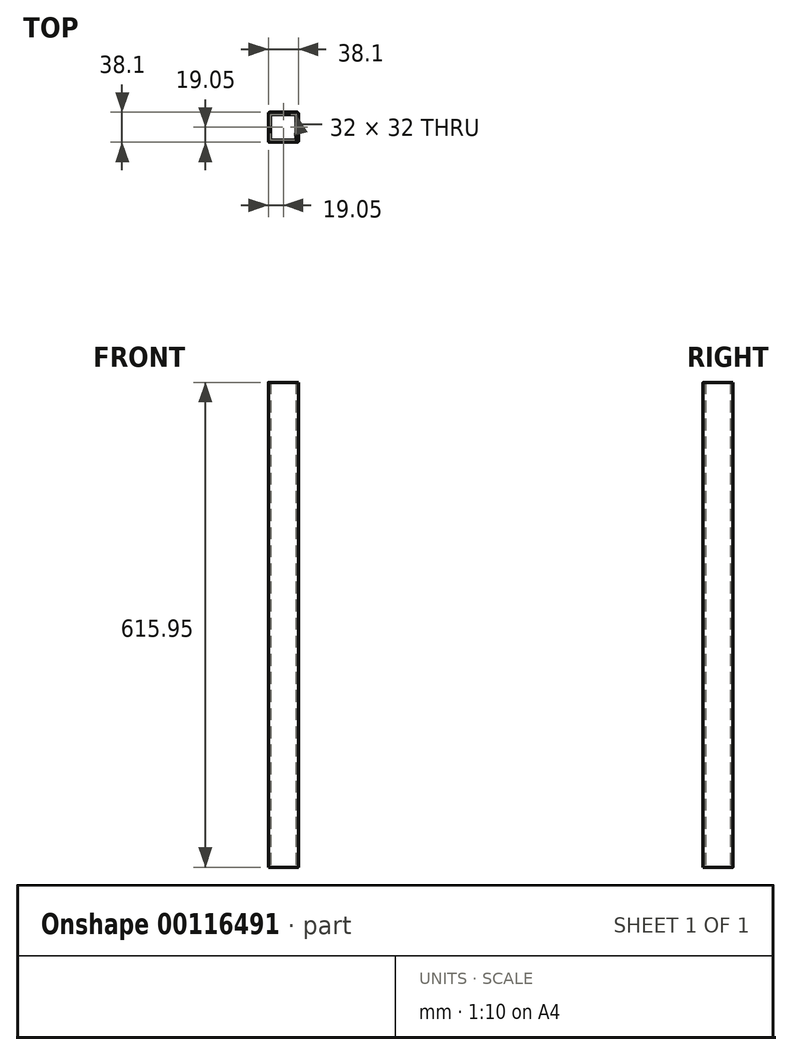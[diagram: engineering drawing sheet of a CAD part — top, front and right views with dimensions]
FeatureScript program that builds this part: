
annotation { "Feature Type Name" : "Feature", "Feature Type Description" : "" }
export const myFeature = defineFeature(function(context is Context, id is Id, definition is map)
    precondition{}
    {
        {
            var Q0;
            Q0=qCreatedBy(makeId("Top.planeOp"),FACE);
            var sketch = newSketch(context, id + "F0", { "sketchPlane" : qUnion([Q0])});
            skLineSegment(sketch, "E0.bottom", {"start": v(0, 0) * mm, "end": v(38.1, 0) * mm});
            skLineSegment(sketch, "E0.top", {"start": v(0, 38.1) * mm, "end": v(38.1, 38.1) * mm});
            skLineSegment(sketch, "E0.left", {"start": v(0, 0) * mm, "end": v(0, 38.1) * mm});
            skLineSegment(sketch, "E0.right", {"start": v(38.1, 0) * mm, "end": v(38.1, 38.1) * mm});
            skLineSegment(sketch, "E1.0", {"start": v(3.05, 3.05) * mm, "end": v(3.05, 35.05) * mm});
            skLineSegment(sketch, "E1.1", {"start": v(3.05, 3.05) * mm, "end": v(35.05, 3.05) * mm});
            skLineSegment(sketch, "E1.2", {"start": v(35.05, 3.05) * mm, "end": v(35.05, 35.05) * mm});
            skLineSegment(sketch, "E1.3", {"start": v(3.05, 35.05) * mm, "end": v(35.05, 35.05) * mm});
            skSolve(sketch);
        }
        {
            var Q0;
            Q0=makeQuery(id+"F0.imprint","IMPRINT",FACE,{"disambiguationData":[TD([[makeQuery(id+"F0.imprint","IMPRINT",EDGE,{"derivedFrom":sQuery(id+"F0.wireOp",EDGE,"E0.bottom")}),1.0]])]});
            extrude(context, id + "F1", {"entities" : qUnion([Q0]), "depth" : 615.95 * mm});
        }
        {
            var Q0;
            Q0=makeQuery(id+"F1.opExtrude","SWEPT_EDGE",EDGE,{"disambiguationData":[OSD([sQuery(id+"F0.wireOp",EDGE,"E0.top"),sQuery(id+"F0.wireOp",EDGE,"E0.left")])]});
            var Q1;
            Q1=makeQuery(id+"F1.opExtrude","SWEPT_EDGE",EDGE,{"disambiguationData":[OSD([sQuery(id+"F0.wireOp",EDGE,"E0.top"),sQuery(id+"F0.wireOp",EDGE,"E0.right")])]});
            var Q2;
            Q2=makeQuery(id+"F1.opExtrude","SWEPT_EDGE",EDGE,{"disambiguationData":[OSD([sQuery(id+"F0.wireOp",EDGE,"E0.bottom"),sQuery(id+"F0.wireOp",EDGE,"E0.left")])]});
            var Q3;
            Q3=makeQuery(id+"F1.opExtrude","SWEPT_EDGE",EDGE,{"disambiguationData":[OSD([sQuery(id+"F0.wireOp",EDGE,"E0.bottom"),sQuery(id+"F0.wireOp",EDGE,"E0.right")])]});
            fillet(context, id + "F2", {"entities" : qUnion([Q0, Q1, Q2, Q3]), "radius" : 1.52 * mm, "tangentPropagation" : true, "allowEdgeOverflow" : false});
        }
    });
